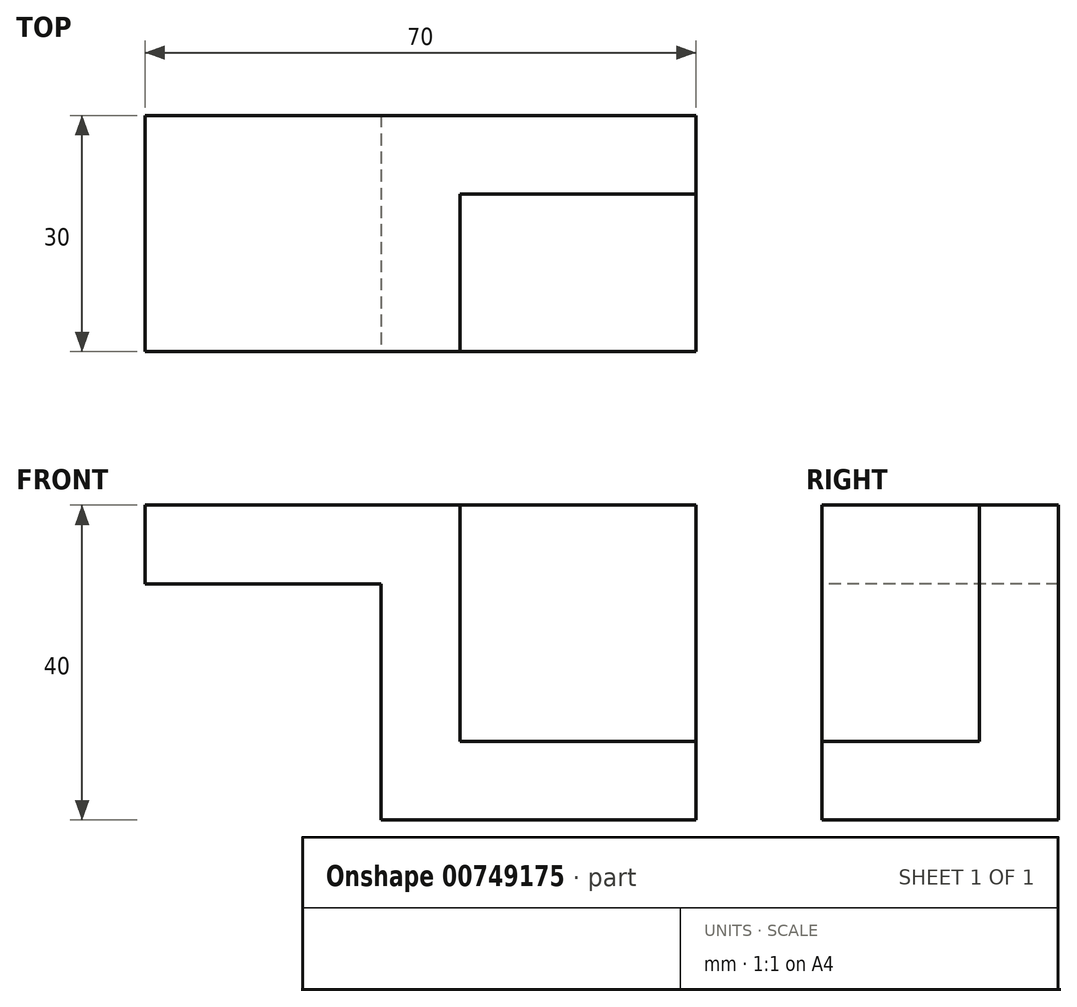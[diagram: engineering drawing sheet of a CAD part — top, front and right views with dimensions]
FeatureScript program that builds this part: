
annotation { "Feature Type Name" : "Feature", "Feature Type Description" : "" }
export const myFeature = defineFeature(function(context is Context, id is Id, definition is map)
    precondition{}
    {
        {
            var Q0;
            Q0=qCreatedBy(makeId("Top.planeOp"),FACE);
            var sketch = newSketch(context, id + "F0", { "sketchPlane" : qUnion([Q0])});
            skLineSegment(sketch, "E0.bottom", {"start": v(0, 0) * mm, "end": v(70, 0) * mm});
            skLineSegment(sketch, "E0.top", {"start": v(0, 30) * mm, "end": v(70, 30) * mm});
            skLineSegment(sketch, "E0.left", {"start": v(0, 0) * mm, "end": v(0, 30) * mm});
            skLineSegment(sketch, "E0.right", {"start": v(70, 0) * mm, "end": v(70, 30) * mm});
            skSolve(sketch);
        }
        {
            var Q0;
            Q0=makeQuery(id+"F0.imprint","IMPRINT",FACE,{"disambiguationData":[TD([[makeQuery(id+"F0.imprint","IMPRINT",EDGE,{"derivedFrom":sQuery(id+"F0.wireOp",EDGE,"E0.bottom")}),1.0]])]});
            extrude(context, id + "F1", {"entities" : qUnion([Q0]), "oppositeDirection" : true, "depth" : 40 * mm, "offsetDistance" : 25 * mm});
        }
        {
            var Q0;
            Q0=qCreatedBy(makeId("Top.planeOp"),FACE);
            var sketch = newSketch(context, id + "F2", { "sketchPlane" : qUnion([Q0])});
            skLineSegment(sketch, "E1.bottom", {"start": v(40, 0) * mm, "end": v(70, 0) * mm});
            skLineSegment(sketch, "E1.top", {"start": v(40, 20) * mm, "end": v(70, 20) * mm});
            skLineSegment(sketch, "E1.left", {"start": v(40, 0) * mm, "end": v(40, 20) * mm});
            skLineSegment(sketch, "E1.right", {"start": v(70, 0) * mm, "end": v(70, 20) * mm});
            skSolve(sketch);
        }
        {
            var Q0;
            Q0 = qSketchRegion(id + "F2", true);
            extrude(context, id + "F3", {"entities" : qUnion([Q0]), "operationType" : NewBodyOperationType.REMOVE, "oppositeDirection" : true, "depth" : 30 * mm, "offsetDistance" : 25 * mm});
        }
        {
            var Q0;
            Q0=qCreatedBy(makeId("Front.planeOp"),FACE);
            var sketch = newSketch(context, id + "F4", { "sketchPlane" : qUnion([Q0])});
            skLineSegment(sketch, "E2", {"start": v(0, -40) * mm, "end": v(30, -40) * mm});
            skLineSegment(sketch, "E3", {"start": v(30, -40) * mm, "end": v(30, -10) * mm});
            skLineSegment(sketch, "E4", {"start": v(30, -10) * mm, "end": v(0, -10) * mm});
            skLineSegment(sketch, "E5", {"start": v(0, -10) * mm, "end": v(0, -40) * mm});
            skSolve(sketch);
        }
        {
            var Q0;
            Q0 = qSketchRegion(id + "F4", true);
            extrude(context, id + "F5", {"entities" : qUnion([Q0]), "operationType" : NewBodyOperationType.REMOVE, "endBound" : BoundingType.THROUGH_ALL, "oppositeDirection" : true, "depth" : 25 * mm, "offsetDistance" : 25 * mm});
        }
    });
